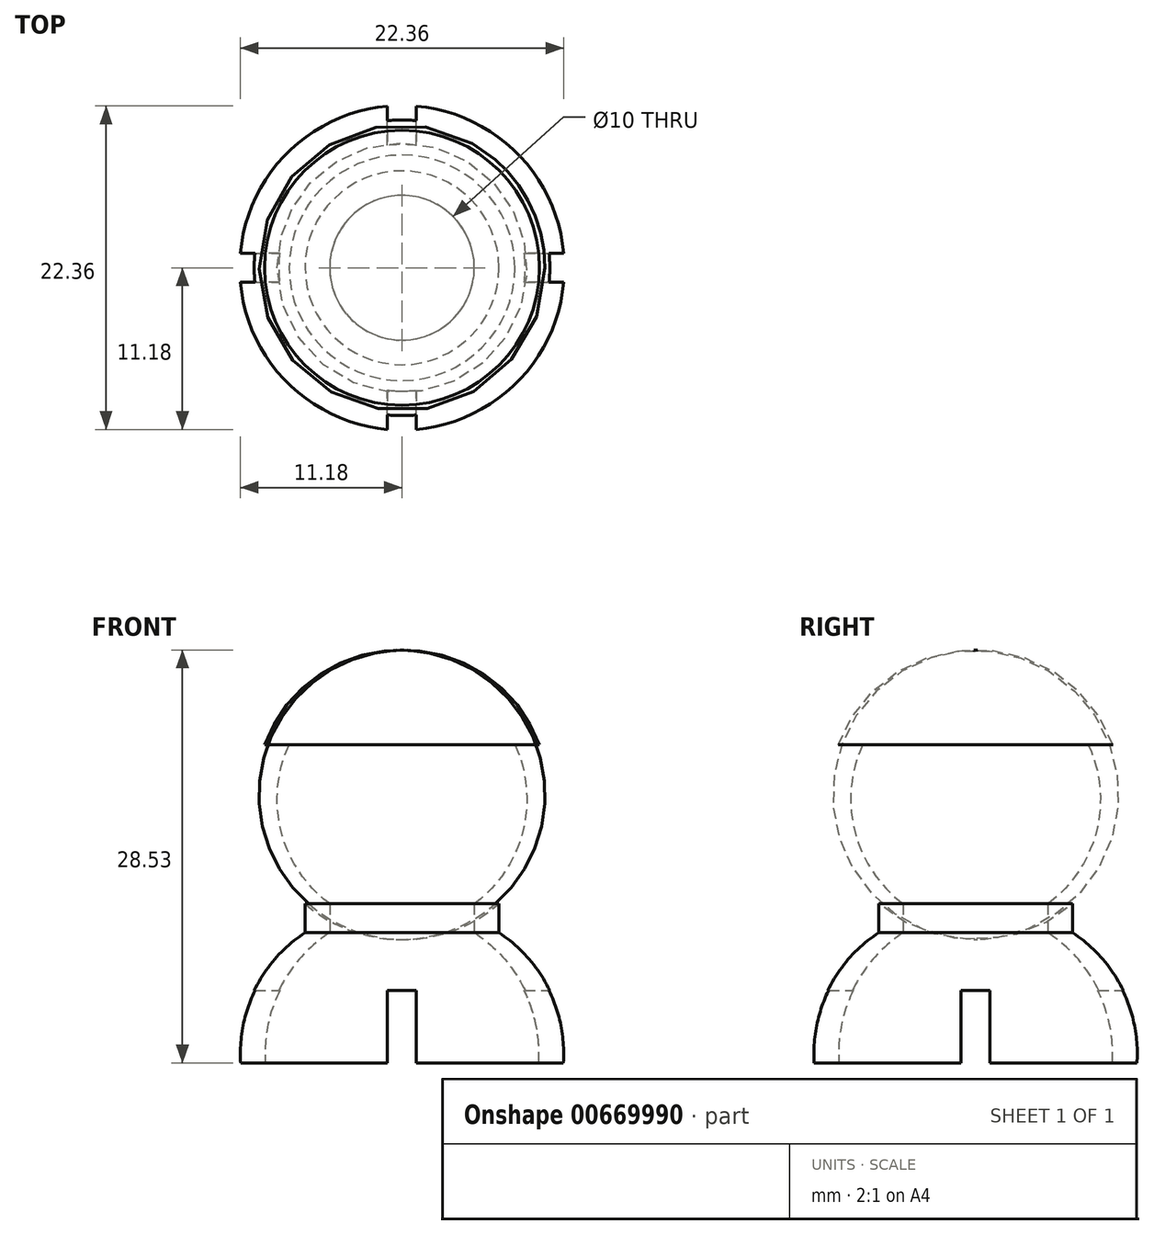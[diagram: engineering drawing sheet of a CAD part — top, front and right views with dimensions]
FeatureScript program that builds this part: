
annotation { "Feature Type Name" : "Feature", "Feature Type Description" : "" }
export const myFeature = defineFeature(function(context is Context, id is Id, definition is map)
    precondition{}
    {
        {
            var Q0;
            Q0=qCreatedBy(makeId("Front.planeOp"),FACE);
            var sketch = newSketch(context, id + "F0", { "sketchPlane" : qUnion([Q0])});
            skLineSegment(sketch, "E0", {"start": v(0, 0) * mm, "end": v(0, 3.5) * mm, "construction": true});
            skArc(sketch, "E1", {"start": v(5, 0) * mm, "mid": v(8.35, 5) * mm, "end": v(7.8, 11) * mm});
            skLineSegment(sketch, "E2", {"start": v(5, 0) * mm, "end": v(5, -2) * mm});
            skArc(sketch, "E3", {"start": v(9.5, -11) * mm, "mid": v(8.46, -5.9) * mm, "end": v(5, -2) * mm});
            skArc(sketch, "E4", {"start": v(6.7, 0) * mm, "mid": v(9.81, 5.06) * mm, "end": v(9.5, 11) * mm});
            skArc(sketch, "E5", {"start": v(11.2, -11) * mm, "mid": v(10.16, -5.9) * mm, "end": v(6.7, -2) * mm});
            skLineSegment(sketch, "E6", {"start": v(6.7, 0) * mm, "end": v(6.7, -2) * mm});
            skLineSegment(sketch, "E7", {"start": v(7.8, 11) * mm, "end": v(9.5, 11) * mm});
            skLineSegment(sketch, "E8", {"start": v(9.5, -11) * mm, "end": v(11.2, -11) * mm});
            skSolve(sketch);
        }
        {
            var Q0;
            Q0 = qSketchRegion(id + "F0", true);
            var Q1;
            Q1=sQuery(id+"F0.wireOp",EDGE,"E0");
            revolve(context, id + "F1", {"entities" : qUnion([Q0]), "axis" : qUnion([Q1]), "revolveType" : RevolveType.FULL});
        }
        {
            var Q0;
            Q0=makeQuery(id+"F1.opRevolve","SWEPT_FACE",FACE,{"disambiguationData":[OSD([sQuery(id+"F0.wireOp",EDGE,"E8")])]});
            var sketch = newSketch(context, id + "F2", { "sketchPlane" : qUnion([Q0])});
            skLineSegment(sketch, "E9.bottom", {"start": v(-12.34, 1) * mm, "end": v(12.34, 1) * mm});
            skLineSegment(sketch, "E9.top", {"start": v(-12.34, -1) * mm, "end": v(12.34, -1) * mm});
            skLineSegment(sketch, "E9.left", {"start": v(-12.34, 1) * mm, "end": v(-12.34, -1) * mm});
            skLineSegment(sketch, "E9.right", {"start": v(12.34, 1) * mm, "end": v(12.34, -1) * mm});
            skLineSegment(sketch, "E10.bottom", {"start": v(-1, 12.34) * mm, "end": v(1, 12.34) * mm});
            skLineSegment(sketch, "E10.top", {"start": v(-1, -12.34) * mm, "end": v(1, -12.34) * mm});
            skLineSegment(sketch, "E10.left", {"start": v(-1, 12.34) * mm, "end": v(-1, -12.34) * mm});
            skLineSegment(sketch, "E10.right", {"start": v(1, 12.34) * mm, "end": v(1, -12.34) * mm});
            skSolve(sketch);
        }
        {
            var Q0;
            Q0 = qSketchRegion(id + "F2", true);
            extrude(context, id + "F3", {"entities" : qUnion([Q0]), "operationType" : NewBodyOperationType.REMOVE, "oppositeDirection" : true, "depth" : 5 * mm, "offsetDistance" : 25 * mm});
        }
    });
